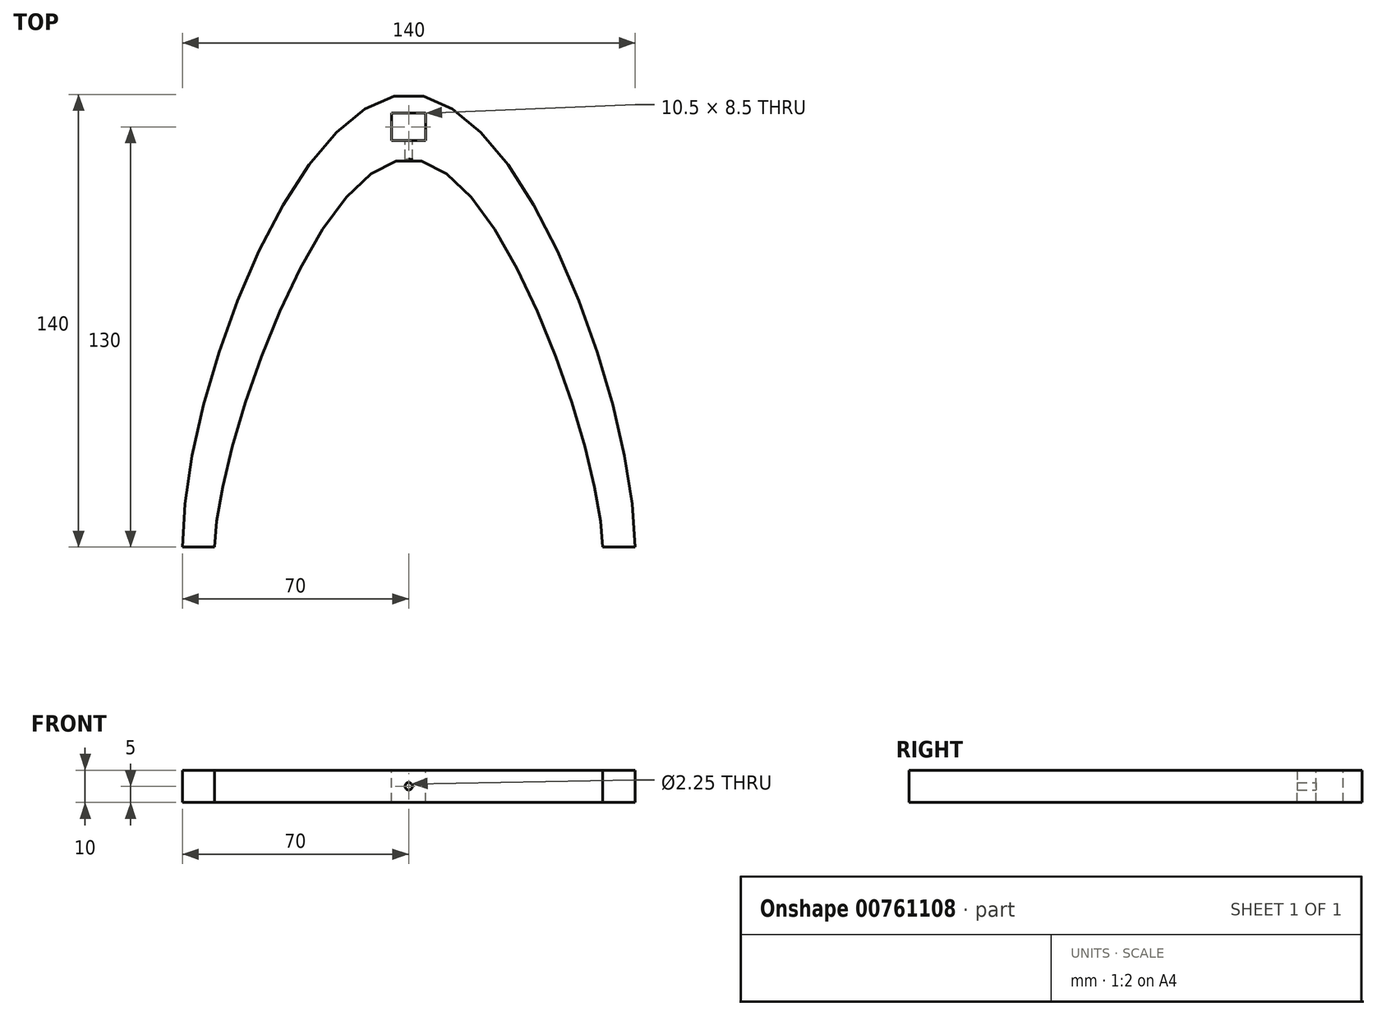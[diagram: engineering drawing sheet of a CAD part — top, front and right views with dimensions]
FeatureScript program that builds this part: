
annotation { "Feature Type Name" : "Feature", "Feature Type Description" : "" }
export const myFeature = defineFeature(function(context is Context, id is Id, definition is map)
    precondition{}
    {
        {
            var Q0;
            Q0=qCreatedBy(makeId("Top.planeOp"),FACE);
            var sketch = newSketch(context, id + "F0", { "sketchPlane" : qUnion([Q0])});
            skFitSpline(sketch, "E0", {"points": [v(-70, -120) * mm, v(0, 20) * mm, v(70, -120) * mm], "startDerivative": vector(0.3, 286.62) * mm, "endDerivative": vector(4.76, -286.62) * mm});
            skLineSegment(sketch, "E1", {"start": v(-70, -120) * mm, "end": v(70, -120) * mm, "construction": true});
            skLineSegment(sketch, "E2", {"start": v(-70, -120) * mm, "end": v(-60, -120) * mm});
            skLineSegment(sketch, "E3", {"start": v(70, -120) * mm, "end": v(60, -120) * mm});
            skFitSpline(sketch, "E4", {"points": [v(-60, -120) * mm, v(0, 0) * mm, v(60, -120) * mm], "startDerivative": vector(-1.66, 151.95) * mm, "endDerivative": vector(-0.38, -151.95) * mm});
            skLineSegment(sketch, "E5", {"start": v(-69.95, -72.23) * mm, "end": v(69.2, -72.23) * mm, "construction": true});
            skLineSegment(sketch, "E6", {"start": v(-60.28, -94.68) * mm, "end": v(60.06, -94.68) * mm, "construction": true});
            skSolve(sketch);
        }
        {
            var Q0;
            Q0=makeQuery(id+"F0.imprint","IMPRINT",FACE,{"disambiguationData":[TD([[makeQuery(id+"F0.imprint","IMPRINT",EDGE,{"derivedFrom":sQuery(id+"F0.wireOp",EDGE,"E0")}),-1.0]])]});
            extrude(context, id + "F1", {"entities" : qUnion([Q0]), "depth" : 10 * mm, "offsetDistance" : 25 * mm});
        }
        {
            var Q0;
            Q0=makeQuery(id+"F1.opExtrude","CAP_FACE",FACE,{"disambiguationData":[OSD([sQuery(id+"F0.wireOp",EDGE,"E0"),sQuery(id+"F0.wireOp",EDGE,"E2"),sQuery(id+"F0.wireOp",EDGE,"E3"),sQuery(id+"F0.wireOp",EDGE,"E4")])],"isStart":false});
            var sketch = newSketch(context, id + "F2", { "sketchPlane" : qUnion([Q0])});
            skLineSegment(sketch, "E7", {"start": v(5.25, 5.75) * mm, "end": v(5.25, 14.25) * mm});
            skLineSegment(sketch, "E8", {"start": v(5.25, 14.25) * mm, "end": v(-5.25, 14.25) * mm});
            skLineSegment(sketch, "E9", {"start": v(-5.25, 14.25) * mm, "end": v(-5.25, 5.75) * mm});
            skLineSegment(sketch, "E10", {"start": v(0, 20) * mm, "end": v(0, 0) * mm, "construction": true});
            skLineSegment(sketch, "E11", {"start": v(-5.25, 5.75) * mm, "end": v(0, 10) * mm, "construction": true});
            skLineSegment(sketch, "E12", {"start": v(0, 10) * mm, "end": v(5.25, 14.25) * mm, "construction": true});
            skLineSegment(sketch, "E13", {"start": v(-5.25, 5.75) * mm, "end": v(5.25, 5.75) * mm});
            skSolve(sketch);
        }
        {
            var Q0;
            Q0 = qSketchRegion(id + "F2", true);
            extrude(context, id + "F3", {"entities" : qUnion([Q0]), "operationType" : NewBodyOperationType.REMOVE, "endBound" : BoundingType.UP_TO_NEXT, "oppositeDirection" : true, "depth" : 25 * mm, "offsetDistance" : 25 * mm});
        }
        {
            var Q0;
            Q0=makeQuery(id+"F3.boolean.opBoolean","COPY",FACE,{"derivedFrom":makeQuery(id+"F3.opExtrude","SWEPT_FACE",FACE,{"disambiguationData":[OSD([sQuery(id+"F2.wireOp",EDGE,"E13")])]})});
            var sketch = newSketch(context, id + "F4", { "sketchPlane" : qUnion([Q0])});
            skCircle(sketch, "E14", {"center": v(0, 5) * mm, "radius": 1.13 * mm});
            skLineSegment(sketch, "E15", {"start": v(5.25, 0) * mm, "end": v(-5.25, 10) * mm, "construction": true});
            skSolve(sketch);
        }
        {
            var Q0;
            Q0 = qSketchRegion(id + "F4", true);
            extrude(context, id + "F5", {"entities" : qUnion([Q0]), "operationType" : NewBodyOperationType.REMOVE, "endBound" : BoundingType.UP_TO_NEXT, "oppositeDirection" : true, "depth" : 25 * mm, "offsetDistance" : 25 * mm});
        }
    });
